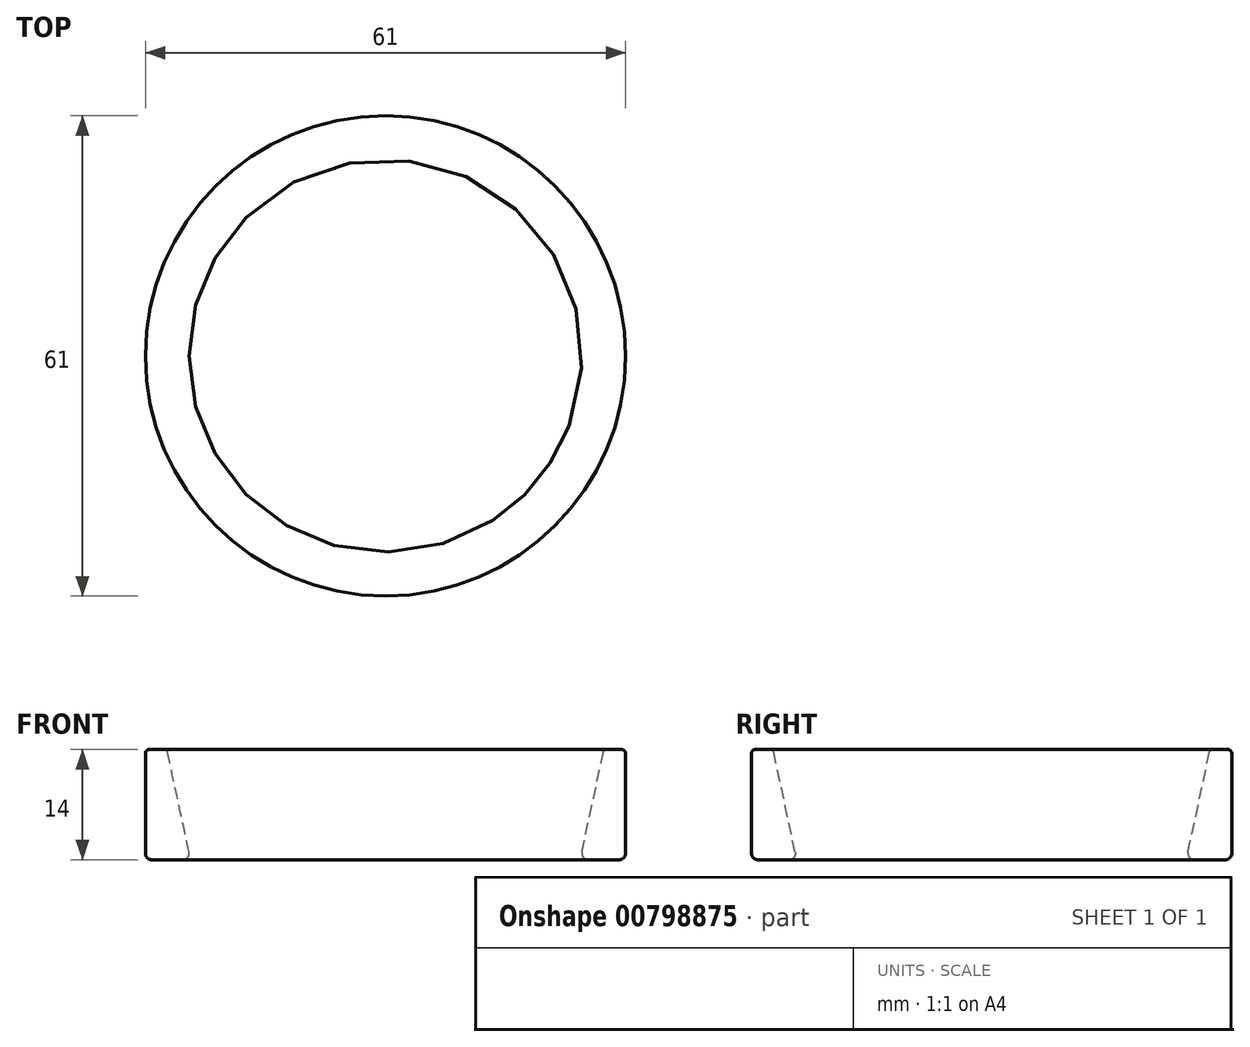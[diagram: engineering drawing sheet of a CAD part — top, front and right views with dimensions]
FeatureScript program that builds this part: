
annotation { "Feature Type Name" : "Feature", "Feature Type Description" : "" }
export const myFeature = defineFeature(function(context is Context, id is Id, definition is map)
    precondition{}
    {
        {
            var Q0;
            Q0=qCreatedBy(makeId("Front.planeOp"),FACE);
            var sketch = newSketch(context, id + "F0", { "sketchPlane" : qUnion([Q0])});
            skLineSegment(sketch, "E0", {"start": v(0, 0) * mm, "end": v(0, 26.04) * mm, "construction": true});
            skLineSegment(sketch, "E1", {"start": v(0, 0) * mm, "end": v(-32.41, 0) * mm, "construction": true});
            skLineSegment(sketch, "E2", {"start": v(-29.7, 0) * mm, "end": v(-25.74, 0) * mm});
            skLineSegment(sketch, "E3", {"start": v(-24.96, 0.97) * mm, "end": v(-27.67, 13.6) * mm});
            skLineSegment(sketch, "E4", {"start": v(-28.15, 14) * mm, "end": v(-30, 14) * mm});
            skLineSegment(sketch, "E5", {"start": v(-30.5, 13.5) * mm, "end": v(-30.5, 0.8) * mm});
            skPoint(sketch, "E6.visualSharp", {"position": v(-30.5, 0) * mm});
            skArc(sketch, "E6.filletArc", {"start": v(-30.5, 0.8) * mm, "mid": v(-30.27, 0.23) * mm, "end": v(-29.7, 0) * mm});
            skPoint(sketch, "E7.visualSharp", {"position": v(-24.75, 0) * mm});
            skArc(sketch, "E7.filletArc", {"start": v(-25.74, 0) * mm, "mid": v(-25.12, 0.3) * mm, "end": v(-24.96, 0.97) * mm});
            skPoint(sketch, "E8.visualSharp", {"position": v(-30.5, 14) * mm});
            skArc(sketch, "E8.filletArc", {"start": v(-30, 14) * mm, "mid": v(-30.35, 13.85) * mm, "end": v(-30.5, 13.5) * mm});
            skPoint(sketch, "E9.visualSharp", {"position": v(-27.75, 14) * mm});
            skArc(sketch, "E9.filletArc", {"start": v(-27.67, 13.6) * mm, "mid": v(-27.84, 13.89) * mm, "end": v(-28.15, 14) * mm});
            skSolve(sketch);
        }
        {
            var Q0;
            Q0=makeQuery(id+"F0.imprint","IMPRINT",FACE,{"disambiguationData":[TD([[makeQuery(id+"F0.imprint","IMPRINT",EDGE,{"derivedFrom":sQuery(id+"F0.wireOp",EDGE,"E2")}),1.0]])]});
            var Q1;
            Q1=sQuery(id+"F0.wireOp",EDGE,"E0");
            revolve(context, id + "F1", {"surfaceOperationType" : NewSurfaceOperationType.NEW, "entities" : qUnion([Q0]), "axis" : qUnion([Q1]), "revolveType" : RevolveType.FULL});
        }
    });
